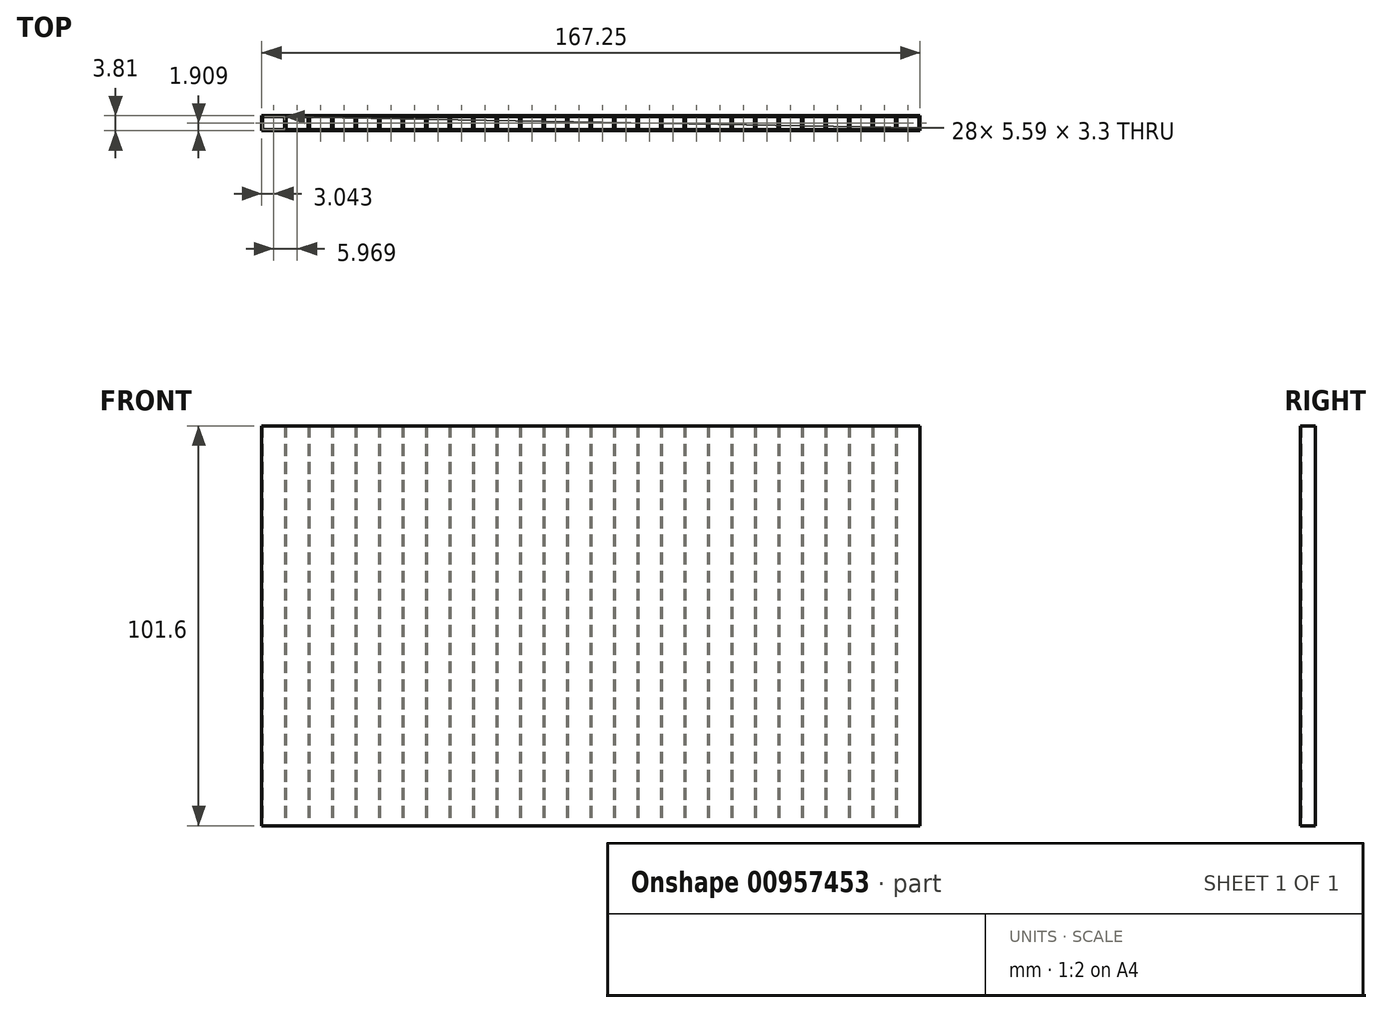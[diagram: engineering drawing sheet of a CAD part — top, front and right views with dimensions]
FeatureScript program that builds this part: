
annotation { "Feature Type Name" : "Feature", "Feature Type Description" : "" }
export const myFeature = defineFeature(function(context is Context, id is Id, definition is map)
    precondition{}
    {
        {
            var Q0;
            Q0=qCreatedBy(makeId("Top.planeOp"),FACE);
            var sketch = newSketch(context, id + "F0", { "sketchPlane" : qUnion([Q0])});
            skLineSegment(sketch, "E0.bottom", {"start": v(1.37, 3.47) * mm, "end": v(6.96, 3.47) * mm});
            skLineSegment(sketch, "E0.top", {"start": v(1.37, 0.17) * mm, "end": v(6.96, 0.17) * mm});
            skLineSegment(sketch, "E0.left", {"start": v(1.37, 3.47) * mm, "end": v(1.37, 0.17) * mm});
            skLineSegment(sketch, "E0.right", {"start": v(6.96, 3.47) * mm, "end": v(6.96, 0.17) * mm});
            skLineSegment(sketch, "E1.1.0.0", {"start": v(7.34, 0.17) * mm, "end": v(12.93, 0.17) * mm});
            skLineSegment(sketch, "E1.1.0.1", {"start": v(12.93, 3.47) * mm, "end": v(12.93, 0.17) * mm});
            skLineSegment(sketch, "E1.1.0.2", {"start": v(7.34, 3.47) * mm, "end": v(7.34, 0.17) * mm});
            skLineSegment(sketch, "E1.1.0.3", {"start": v(7.34, 3.47) * mm, "end": v(12.93, 3.47) * mm});
            skLineSegment(sketch, "E1.2.0.0", {"start": v(13.3, 0.17) * mm, "end": v(18.9, 0.17) * mm});
            skLineSegment(sketch, "E1.2.0.1", {"start": v(18.9, 3.47) * mm, "end": v(18.9, 0.17) * mm});
            skLineSegment(sketch, "E1.2.0.2", {"start": v(13.3, 3.47) * mm, "end": v(13.3, 0.17) * mm});
            skLineSegment(sketch, "E1.2.0.3", {"start": v(13.3, 3.47) * mm, "end": v(18.9, 3.47) * mm});
            skLineSegment(sketch, "E1.3.0.0", {"start": v(19.28, 0.17) * mm, "end": v(24.86, 0.17) * mm});
            skLineSegment(sketch, "E1.3.0.1", {"start": v(24.86, 3.47) * mm, "end": v(24.86, 0.17) * mm});
            skLineSegment(sketch, "E1.3.0.2", {"start": v(19.28, 3.47) * mm, "end": v(19.28, 0.17) * mm});
            skLineSegment(sketch, "E1.3.0.3", {"start": v(19.28, 3.47) * mm, "end": v(24.86, 3.47) * mm});
            skLineSegment(sketch, "E1.4.0.0", {"start": v(25.25, 0.17) * mm, "end": v(30.83, 0.17) * mm});
            skLineSegment(sketch, "E1.4.0.1", {"start": v(30.83, 3.47) * mm, "end": v(30.83, 0.17) * mm});
            skLineSegment(sketch, "E1.4.0.2", {"start": v(25.25, 3.47) * mm, "end": v(25.25, 0.17) * mm});
            skLineSegment(sketch, "E1.4.0.3", {"start": v(25.25, 3.47) * mm, "end": v(30.83, 3.47) * mm});
            skLineSegment(sketch, "E1.5.0.0", {"start": v(31.21, 0.17) * mm, "end": v(36.8, 0.17) * mm});
            skLineSegment(sketch, "E1.5.0.1", {"start": v(36.8, 3.47) * mm, "end": v(36.8, 0.17) * mm});
            skLineSegment(sketch, "E1.5.0.2", {"start": v(31.21, 3.47) * mm, "end": v(31.21, 0.17) * mm});
            skLineSegment(sketch, "E1.5.0.3", {"start": v(31.21, 3.47) * mm, "end": v(36.8, 3.47) * mm});
            skLineSegment(sketch, "E1.6.0.0", {"start": v(37.18, 0.17) * mm, "end": v(42.77, 0.17) * mm});
            skLineSegment(sketch, "E1.6.0.1", {"start": v(42.77, 3.47) * mm, "end": v(42.77, 0.17) * mm});
            skLineSegment(sketch, "E1.6.0.2", {"start": v(37.18, 3.47) * mm, "end": v(37.18, 0.17) * mm});
            skLineSegment(sketch, "E1.6.0.3", {"start": v(37.18, 3.47) * mm, "end": v(42.77, 3.47) * mm});
            skLineSegment(sketch, "E1.7.0.0", {"start": v(43.15, 0.17) * mm, "end": v(48.74, 0.17) * mm});
            skLineSegment(sketch, "E1.7.0.1", {"start": v(48.74, 3.47) * mm, "end": v(48.74, 0.17) * mm});
            skLineSegment(sketch, "E1.7.0.2", {"start": v(43.15, 3.47) * mm, "end": v(43.15, 0.17) * mm});
            skLineSegment(sketch, "E1.7.0.3", {"start": v(43.15, 3.47) * mm, "end": v(48.74, 3.47) * mm});
            skLineSegment(sketch, "E1.8.0.0", {"start": v(49.12, 0.17) * mm, "end": v(54.7, 0.17) * mm});
            skLineSegment(sketch, "E1.8.0.1", {"start": v(54.7, 3.47) * mm, "end": v(54.7, 0.17) * mm});
            skLineSegment(sketch, "E1.8.0.2", {"start": v(49.12, 3.47) * mm, "end": v(49.12, 0.17) * mm});
            skLineSegment(sketch, "E1.8.0.3", {"start": v(49.12, 3.47) * mm, "end": v(54.7, 3.47) * mm});
            skLineSegment(sketch, "E1.9.0.0", {"start": v(55.1, 0.17) * mm, "end": v(60.68, 0.17) * mm});
            skLineSegment(sketch, "E1.9.0.1", {"start": v(60.68, 3.47) * mm, "end": v(60.68, 0.17) * mm});
            skLineSegment(sketch, "E1.9.0.2", {"start": v(55.1, 3.47) * mm, "end": v(55.1, 0.17) * mm});
            skLineSegment(sketch, "E1.9.0.3", {"start": v(55.1, 3.47) * mm, "end": v(60.68, 3.47) * mm});
            skLineSegment(sketch, "E1.10.0.0", {"start": v(61.06, 0.17) * mm, "end": v(66.65, 0.17) * mm});
            skLineSegment(sketch, "E1.10.0.1", {"start": v(66.65, 3.47) * mm, "end": v(66.65, 0.17) * mm});
            skLineSegment(sketch, "E1.10.0.2", {"start": v(61.06, 3.47) * mm, "end": v(61.06, 0.17) * mm});
            skLineSegment(sketch, "E1.10.0.3", {"start": v(61.06, 3.47) * mm, "end": v(66.65, 3.47) * mm});
            skLineSegment(sketch, "E1.11.0.0", {"start": v(67.03, 0.17) * mm, "end": v(72.62, 0.17) * mm});
            skLineSegment(sketch, "E1.11.0.1", {"start": v(72.62, 3.47) * mm, "end": v(72.62, 0.17) * mm});
            skLineSegment(sketch, "E1.11.0.2", {"start": v(67.03, 3.47) * mm, "end": v(67.03, 0.17) * mm});
            skLineSegment(sketch, "E1.11.0.3", {"start": v(67.03, 3.47) * mm, "end": v(72.62, 3.47) * mm});
            skLineSegment(sketch, "E1.12.0.0", {"start": v(73, 0.17) * mm, "end": v(78.59, 0.17) * mm});
            skLineSegment(sketch, "E1.12.0.1", {"start": v(78.59, 3.47) * mm, "end": v(78.59, 0.17) * mm});
            skLineSegment(sketch, "E1.12.0.2", {"start": v(73, 3.47) * mm, "end": v(73, 0.17) * mm});
            skLineSegment(sketch, "E1.12.0.3", {"start": v(73, 3.47) * mm, "end": v(78.59, 3.47) * mm});
            skLineSegment(sketch, "E1.13.0.0", {"start": v(78.97, 0.17) * mm, "end": v(84.55, 0.17) * mm});
            skLineSegment(sketch, "E1.13.0.1", {"start": v(84.55, 3.47) * mm, "end": v(84.55, 0.17) * mm});
            skLineSegment(sketch, "E1.13.0.2", {"start": v(78.97, 3.47) * mm, "end": v(78.97, 0.17) * mm});
            skLineSegment(sketch, "E1.13.0.3", {"start": v(78.97, 3.47) * mm, "end": v(84.55, 3.47) * mm});
            skLineSegment(sketch, "E1.14.0.0", {"start": v(84.94, 0.17) * mm, "end": v(90.52, 0.17) * mm});
            skLineSegment(sketch, "E1.14.0.1", {"start": v(90.52, 3.47) * mm, "end": v(90.52, 0.17) * mm});
            skLineSegment(sketch, "E1.14.0.2", {"start": v(84.94, 3.47) * mm, "end": v(84.94, 0.17) * mm});
            skLineSegment(sketch, "E1.14.0.3", {"start": v(84.94, 3.47) * mm, "end": v(90.52, 3.47) * mm});
            skLineSegment(sketch, "E1.15.0.0", {"start": v(90.9, 0.17) * mm, "end": v(96.5, 0.17) * mm});
            skLineSegment(sketch, "E1.15.0.1", {"start": v(96.5, 3.47) * mm, "end": v(96.5, 0.17) * mm});
            skLineSegment(sketch, "E1.15.0.2", {"start": v(90.9, 3.47) * mm, "end": v(90.9, 0.17) * mm});
            skLineSegment(sketch, "E1.15.0.3", {"start": v(90.9, 3.47) * mm, "end": v(96.5, 3.47) * mm});
            skLineSegment(sketch, "E1.16.0.0", {"start": v(96.87, 0.17) * mm, "end": v(102.46, 0.17) * mm});
            skLineSegment(sketch, "E1.16.0.1", {"start": v(102.46, 3.47) * mm, "end": v(102.46, 0.17) * mm});
            skLineSegment(sketch, "E1.16.0.2", {"start": v(96.87, 3.47) * mm, "end": v(96.87, 0.17) * mm});
            skLineSegment(sketch, "E1.16.0.3", {"start": v(96.87, 3.47) * mm, "end": v(102.46, 3.47) * mm});
            skLineSegment(sketch, "E1.17.0.0", {"start": v(102.84, 0.17) * mm, "end": v(108.43, 0.17) * mm});
            skLineSegment(sketch, "E1.17.0.1", {"start": v(108.43, 3.47) * mm, "end": v(108.43, 0.17) * mm});
            skLineSegment(sketch, "E1.17.0.2", {"start": v(102.84, 3.47) * mm, "end": v(102.84, 0.17) * mm});
            skLineSegment(sketch, "E1.17.0.3", {"start": v(102.84, 3.47) * mm, "end": v(108.43, 3.47) * mm});
            skLineSegment(sketch, "E1.18.0.0", {"start": v(108.81, 0.17) * mm, "end": v(114.4, 0.17) * mm});
            skLineSegment(sketch, "E1.18.0.1", {"start": v(114.4, 3.47) * mm, "end": v(114.4, 0.17) * mm});
            skLineSegment(sketch, "E1.18.0.2", {"start": v(108.81, 3.47) * mm, "end": v(108.81, 0.17) * mm});
            skLineSegment(sketch, "E1.18.0.3", {"start": v(108.81, 3.47) * mm, "end": v(114.4, 3.47) * mm});
            skLineSegment(sketch, "E1.19.0.0", {"start": v(114.78, 0.17) * mm, "end": v(120.37, 0.17) * mm});
            skLineSegment(sketch, "E1.19.0.1", {"start": v(120.37, 3.47) * mm, "end": v(120.37, 0.17) * mm});
            skLineSegment(sketch, "E1.19.0.2", {"start": v(114.78, 3.47) * mm, "end": v(114.78, 0.17) * mm});
            skLineSegment(sketch, "E1.19.0.3", {"start": v(114.78, 3.47) * mm, "end": v(120.37, 3.47) * mm});
            skLineSegment(sketch, "E1.direction1", {"start": v(1.37, 0.17) * mm, "end": v(7.34, 0.17) * mm, "construction": true});
            skLineSegment(sketch, "E2.left", {"start": v(1.12, 3.72) * mm, "end": v(1.12, -0.09) * mm});
            skLineSegment(sketch, "E3.0.20.0", {"start": v(120.75, 0.17) * mm, "end": v(126.34, 0.17) * mm});
            skLineSegment(sketch, "E3.3.20.0", {"start": v(126.34, 3.47) * mm, "end": v(126.34, 0.17) * mm});
            skLineSegment(sketch, "E3.6.20.0", {"start": v(120.75, 3.47) * mm, "end": v(120.75, 0.17) * mm});
            skLineSegment(sketch, "E3.9.20.0", {"start": v(120.75, 3.47) * mm, "end": v(126.34, 3.47) * mm});
            skLineSegment(sketch, "E3.0.21.0", {"start": v(126.72, 0.17) * mm, "end": v(132.3, 0.17) * mm});
            skLineSegment(sketch, "E3.3.21.0", {"start": v(132.3, 3.47) * mm, "end": v(132.3, 0.17) * mm});
            skLineSegment(sketch, "E3.6.21.0", {"start": v(126.72, 3.47) * mm, "end": v(126.72, 0.17) * mm});
            skLineSegment(sketch, "E3.9.21.0", {"start": v(126.72, 3.47) * mm, "end": v(132.3, 3.47) * mm});
            skLineSegment(sketch, "E3.0.22.0", {"start": v(132.69, 0.17) * mm, "end": v(138.28, 0.17) * mm});
            skLineSegment(sketch, "E3.3.22.0", {"start": v(138.28, 3.47) * mm, "end": v(138.28, 0.17) * mm});
            skLineSegment(sketch, "E3.6.22.0", {"start": v(132.69, 3.47) * mm, "end": v(132.69, 0.17) * mm});
            skLineSegment(sketch, "E3.9.22.0", {"start": v(132.69, 3.47) * mm, "end": v(138.28, 3.47) * mm});
            skLineSegment(sketch, "E3.0.23.0", {"start": v(138.66, 0.17) * mm, "end": v(144.24, 0.17) * mm});
            skLineSegment(sketch, "E3.3.23.0", {"start": v(144.24, 3.47) * mm, "end": v(144.24, 0.17) * mm});
            skLineSegment(sketch, "E3.6.23.0", {"start": v(138.66, 3.47) * mm, "end": v(138.66, 0.17) * mm});
            skLineSegment(sketch, "E3.9.23.0", {"start": v(138.66, 3.47) * mm, "end": v(144.24, 3.47) * mm});
            skLineSegment(sketch, "E3.0.24.0", {"start": v(144.63, 0.17) * mm, "end": v(150.21, 0.17) * mm});
            skLineSegment(sketch, "E3.3.24.0", {"start": v(150.21, 3.47) * mm, "end": v(150.21, 0.17) * mm});
            skLineSegment(sketch, "E3.6.24.0", {"start": v(144.63, 3.47) * mm, "end": v(144.63, 0.17) * mm});
            skLineSegment(sketch, "E3.9.24.0", {"start": v(144.63, 3.47) * mm, "end": v(150.21, 3.47) * mm});
            skLineSegment(sketch, "E3.0.25.0", {"start": v(150.6, 0.17) * mm, "end": v(156.18, 0.17) * mm});
            skLineSegment(sketch, "E3.3.25.0", {"start": v(156.18, 3.47) * mm, "end": v(156.18, 0.17) * mm});
            skLineSegment(sketch, "E3.6.25.0", {"start": v(150.6, 3.47) * mm, "end": v(150.6, 0.17) * mm});
            skLineSegment(sketch, "E3.9.25.0", {"start": v(150.6, 3.47) * mm, "end": v(156.18, 3.47) * mm});
            skLineSegment(sketch, "E3.0.26.0", {"start": v(156.56, 0.17) * mm, "end": v(162.15, 0.17) * mm});
            skLineSegment(sketch, "E3.3.26.0", {"start": v(162.15, 3.47) * mm, "end": v(162.15, 0.17) * mm});
            skLineSegment(sketch, "E3.6.26.0", {"start": v(156.56, 3.47) * mm, "end": v(156.56, 0.17) * mm});
            skLineSegment(sketch, "E3.9.26.0", {"start": v(156.56, 3.47) * mm, "end": v(162.15, 3.47) * mm});
            skLineSegment(sketch, "E3.0.27.0", {"start": v(162.53, 0.17) * mm, "end": v(168.12, 0.17) * mm});
            skLineSegment(sketch, "E3.3.27.0", {"start": v(168.12, 3.47) * mm, "end": v(168.12, 0.17) * mm});
            skLineSegment(sketch, "E3.6.27.0", {"start": v(162.53, 3.47) * mm, "end": v(162.53, 0.17) * mm});
            skLineSegment(sketch, "E3.9.27.0", {"start": v(162.53, 3.47) * mm, "end": v(168.12, 3.47) * mm});
            skLineSegment(sketch, "E4", {"start": v(168.12, 4.14) * mm, "end": v(168.37, 4.14) * mm});
            skLineSegment(sketch, "E5", {"start": v(1.12, 3.72) * mm, "end": v(168.37, 3.72) * mm});
            skLineSegment(sketch, "E6", {"start": v(168.37, 3.72) * mm, "end": v(168.37, -0.09) * mm});
            skLineSegment(sketch, "E7", {"start": v(1.12, -0.09) * mm, "end": v(168.37, -0.09) * mm});
            skSolve(sketch);
        }
        {
            var Q0;
            Q0=makeQuery(id+"F0.imprint","IMPRINT",FACE,{"disambiguationData":[TD([[makeQuery(id+"F0.imprint","IMPRINT",EDGE,{"derivedFrom":sQuery(id+"F0.wireOp",EDGE,"E0.bottom")}),1.0]])]});
            extrude(context, id + "F1", {"entities" : qUnion([Q0]), "depth" : 101.6 * mm, "offsetDistance" : 25.4 * mm});
        }
    });
